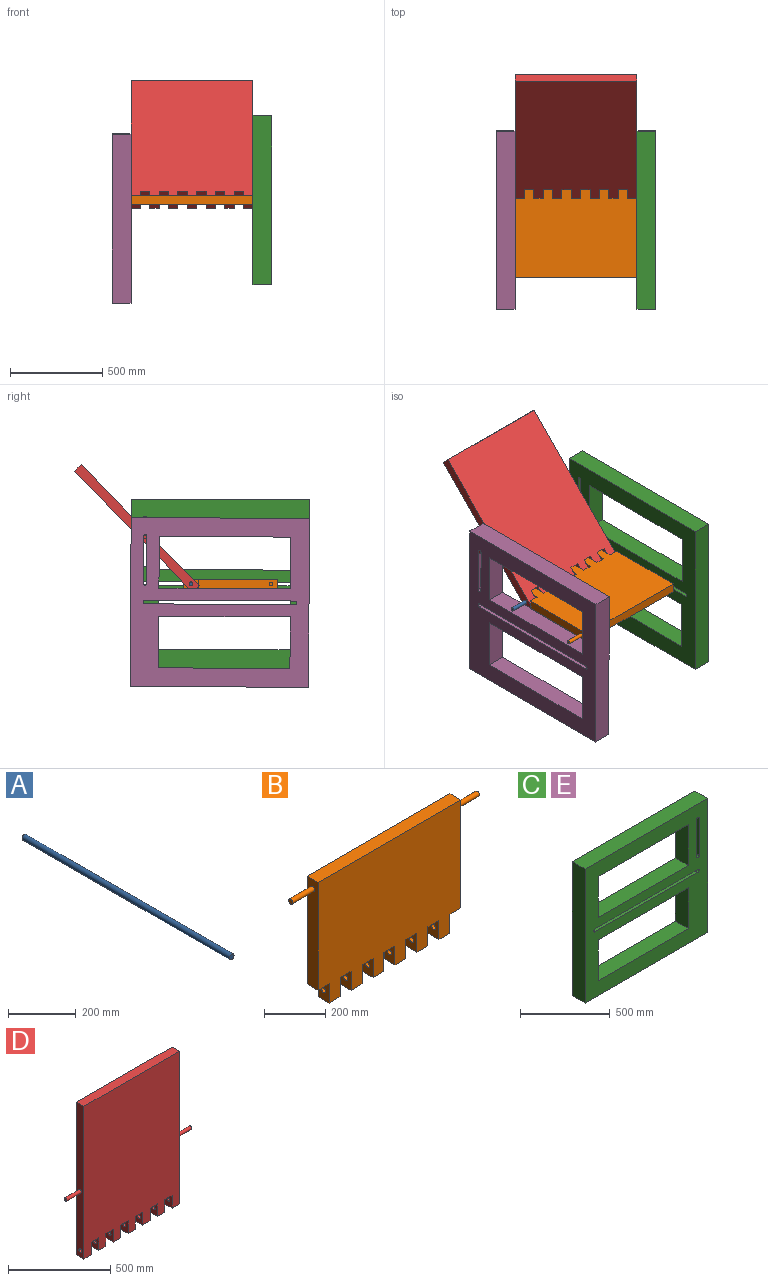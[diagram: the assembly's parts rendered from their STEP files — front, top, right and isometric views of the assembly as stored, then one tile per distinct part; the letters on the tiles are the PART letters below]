
ASSEMBLY  parts=5 mates=9
PART A: 3 faces, bbox 19.1x863.6x19.1 mm
  f0: cylinder r=9.53mm len=863.6mm, axis (0,1,0), area 51684.2mm2, adj f1,f2
  f1: plane 19.05x19.05mm, normal (0,-1,0), area 285mm2, adj f0
  f2: plane 19.05x19.05mm, normal (0,1,0), area 285mm2, adj f0
PART B: 40 faces, bbox 863.6x50.8x508 mm
  f0: plane 76.2x50.8mm, normal (1,0,0), area 3585.9mm2, adj f1,f27,f28,f29,f30
  f1: plane 50.8x50.8mm, normal (0,0,-1), area 2580.6mm2, adj f0,f2,f28,f29
  f2: plane 76.2x50.8mm, normal (-1,0,0), area 3585.9mm2, adj f1,f3,f28,f29,f35
  f3: plane 50.8x50.8mm, normal (0,0,-1), area 2580.6mm2, adj f2,f4,f28,f29
  f4: plane 76.2x50.8mm, normal (1,0,0), area 3585.9mm2, adj f3,f5,f28,f29,f35
  f5: plane 50.8x50.8mm, normal (0,0,-1), area 2580.6mm2, adj f4,f6,f28,f29
  f6: plane 76.2x50.8mm, normal (-1,0,0), area 3585.9mm2, adj f5,f7,f28,f29,f34
  f7: plane 50.8x50.8mm, normal (0,0,-1), area 2580.6mm2, adj f6,f8,f28,f29
  f8: plane 76.2x50.8mm, normal (1,0,0), area 3585.9mm2, adj f7,f9,f28,f29,f34
  f9: plane 50.8x50.8mm, normal (0,0,-1), area 2580.6mm2, adj f8,f10,f28,f29
  f10: plane 76.2x50.8mm, normal (-1,0,0), area 3585.9mm2, adj f9,f11,f28,f29,f33
  f11: plane 50.8x50.8mm, normal (0,0,-1), area 2580.6mm2, adj f10,f12,f28,f29
  f12: plane 76.2x50.8mm, normal (1,0,0), area 3585.9mm2, adj f11,f13,f28,f29,f33
  f13: plane 50.8x50.8mm, normal (0,0,-1), area 2580.6mm2, adj f12,f14,f28,f29
  f14: plane 431.8x50.8mm, normal (1,0,0), area 21650.4mm2, adj f13,f15,f28,f29,f36
  f15: plane 660.4x50.8mm, normal (0,0,1), area 33548.3mm2, adj f14,f16,f28,f29
  f16: plane 431.8x50.8mm, normal (-1,0,0), area 21650.4mm2, adj f15,f17,f28,f29,f38
  f17: plane 50.8x50.8mm, normal (0,0,-1), area 2580.6mm2, adj f16,f18,f28,f29
  f18: plane 76.2x50.8mm, normal (-1,0,0), area 3585.9mm2, adj f17,f19,f28,f29,f32
  f19: plane 50.8x50.8mm, normal (0,0,-1), area 2580.6mm2, adj f18,f20,f28,f29
  f20: plane 76.2x50.8mm, normal (1,0,0), area 3585.9mm2, adj f19,f21,f28,f29,f32
  f21: plane 50.8x50.8mm, normal (0,0,-1), area 2580.6mm2, adj f20,f22,f28,f29
  f22: plane 76.2x50.8mm, normal (-1,0,0), area 3585.9mm2, adj f21,f23,f28,f29,f31
  f23: plane 50.8x50.8mm, normal (0,0,-1), area 2580.6mm2, adj f22,f24,f28,f29
  f24: plane 76.2x50.8mm, normal (1,0,0), area 3585.9mm2, adj f23,f25,f28,f29,f31
  f25: plane 50.8x50.8mm, normal (0,0,-1), area 2580.6mm2, adj f24,f26,f28,f29
  f26: plane 76.2x50.8mm, normal (-1,0,0), area 3585.9mm2, adj f25,f27,f28,f29,f30
  f27: plane 50.8x50.8mm, normal (0,0,-1), area 2580.6mm2, adj f0,f26,f28,f29
  f28: plane 660.4x508mm, normal (0,-1,0), area 308386.5mm2, adj f0,f1,f2,f3,f4,f5,f6,f7
  f29: plane 660.4x508mm, normal (0,1,0), area 308386.5mm2, adj f0,f1,f2,f3,f4,f5,f6,f7
  f30: cylinder r=9.53mm len=50.8mm, axis (1,0,0), area 3040.2mm2, adj f0,f26
  f31: cylinder r=9.53mm len=50.8mm, axis (1,0,0), area 3040.2mm2, adj f22,f24
  f32: cylinder r=9.53mm len=50.8mm, axis (1,0,0), area 3040.2mm2, adj f18,f20
  f33: cylinder r=9.53mm len=50.8mm, axis (1,0,0), area 3040.2mm2, adj f10,f12
  f34: cylinder r=9.53mm len=50.8mm, axis (1,0,0), area 3040.2mm2, adj f6,f8
  f35: cylinder r=9.53mm len=50.8mm, axis (1,0,0), area 3040.2mm2, adj f2,f4
  f36: cylinder r=9.53mm len=101.6mm, axis (-1,0,0), area 6080.5mm2, adj f14,f37
  f37: plane 19.05x19.05mm, normal (1,0,0), area 285mm2, adj f36
  f38: cylinder r=9.53mm len=101.6mm, axis (1,0,0), area 6080.5mm2, adj f16,f39
  f39: plane 19.05x19.05mm, normal (-1,0,0), area 285mm2, adj f38
PART C: 22 faces, bbox 965.2x101.6x914.4 mm
  f0: cylinder r=9.53mm len=101.6mm, axis (0,1,0), area 3040.2mm2, adj f1,f19,f20,f21
  f1: plane 812.8x101.6mm, normal (0,0,1), area 82580.5mm2, adj f0,f2,f20,f21
  f2: cylinder r=9.53mm len=101.6mm, axis (0,1,0), area 3040.2mm2, adj f1,f19,f20,f21
  f3: plane 279.4x101.6mm, normal (-1,0,0), area 28387mm2, adj f4,f15,f20,f21
  f4: plane 711.2x101.6mm, normal (0,0,1), area 72257.9mm2, adj f3,f5,f20,f21
  f5: plane 279.4x101.6mm, normal (1,0,0), area 28387mm2, adj f4,f15,f20,f21
  f6: plane 254x101.6mm, normal (1,0,0), area 25806.4mm2, adj f7,f16,f20,f21
  f7: cylinder r=9.53mm len=101.6mm, axis (0,1,0), area 3040.2mm2, adj f6,f8,f20,f21
  f8: plane 254x101.6mm, normal (-1,0,0), area 25806.4mm2, adj f7,f16,f20,f21
  f9: plane 711.2x101.6mm, normal (0,0,1), area 72257.9mm2, adj f10,f17,f20,f21
  f10: plane 279.4x101.6mm, normal (1,0,0), area 28387mm2, adj f9,f11,f20,f21
  f11: plane 711.2x101.6mm, normal (0,0,-1), area 72257.9mm2, adj f10,f17,f20,f21
  f12: plane 914.4x101.6mm, normal (-1,0,0), area 92903mm2, adj f13,f18,f20,f21
  f13: plane 965.2x101.6mm, normal (0,0,-1), area 98064.3mm2, adj f12,f14,f20,f21
  f14: plane 914.4x101.6mm, normal (1,0,0), area 92903mm2, adj f13,f18,f20,f21
  f15: plane 711.2x101.6mm, normal (0,0,-1), area 72257.9mm2, adj f3,f5,f20,f21
  f16: cylinder r=9.53mm len=101.6mm, axis (0,1,0), area 3040.2mm2, adj f6,f8,f20,f21
  f17: plane 279.4x101.6mm, normal (-1,0,0), area 28387mm2, adj f9,f11,f20,f21
  f18: plane 965.2x101.6mm, normal (0,0,1), area 98064.3mm2, adj f12,f14,f20,f21
  f19: plane 812.8x101.6mm, normal (0,0,-1), area 82580.5mm2, adj f0,f2,f20,f21
  f20: plane 965.2x914.4mm, normal (0,-1,0), area 464267.7mm2, adj f0,f1,f2,f3,f4,f5,f6,f7
  f21: plane 965.2x914.4mm, normal (0,1,0), area 464267.7mm2, adj f0,f1,f2,f3,f4,f5,f6,f7
PART D: 41 faces, bbox 863.6x50.8x914.4 mm
  f0: plane 76.2x50.8mm, normal (-1,0,0), area 3585.9mm2, adj f1,f27,f28,f29,f36
  f1: plane 50.8x50.8mm, normal (0,0,-1), area 2580.6mm2, adj f0,f2,f28,f29
  f2: plane 76.2x50.8mm, normal (1,0,0), area 3585.9mm2, adj f1,f3,f28,f29,f36
  f3: plane 50.8x50.8mm, normal (0,0,-1), area 2580.6mm2, adj f2,f4,f28,f29
  f4: plane 76.2x50.8mm, normal (-1,0,0), area 3585.9mm2, adj f3,f5,f28,f29,f35
  f5: plane 50.8x50.8mm, normal (0,0,-1), area 2580.6mm2, adj f4,f6,f28,f29
  f6: plane 76.2x50.8mm, normal (1,0,0), area 3585.9mm2, adj f5,f7,f28,f29,f35
  f7: plane 50.8x50.8mm, normal (0,0,-1), area 2580.6mm2, adj f6,f8,f28,f29
  f8: plane 76.2x50.8mm, normal (-1,0,0), area 3585.9mm2, adj f7,f9,f28,f29,f34
  f9: plane 50.8x50.8mm, normal (0,0,-1), area 2580.6mm2, adj f8,f10,f28,f29
  f10: plane 914.4x50.8mm, normal (1,0,0), area 45881.5mm2, adj f9,f11,f28,f29,f34,f39
  f11: plane 660.4x50.8mm, normal (0,0,1), area 33548.3mm2, adj f10,f12,f28,f29
  f12: plane 914.4x50.8mm, normal (-1,0,0), area 45881.5mm2, adj f11,f13,f28,f29,f33,f37
  f13: plane 50.8x50.8mm, normal (0,0,-1), area 2580.6mm2, adj f12,f14,f28,f29
  f14: plane 76.2x50.8mm, normal (1,0,0), area 3585.9mm2, adj f13,f15,f28,f29,f33
  f15: plane 50.8x50.8mm, normal (0,0,-1), area 2580.6mm2, adj f14,f16,f28,f29
  f16: plane 76.2x50.8mm, normal (-1,0,0), area 3585.9mm2, adj f15,f17,f28,f29,f32
  f17: plane 50.8x50.8mm, normal (0,0,-1), area 2580.6mm2, adj f16,f18,f28,f29
  f18: plane 76.2x50.8mm, normal (1,0,0), area 3585.9mm2, adj f17,f19,f28,f29,f32
  f19: plane 50.8x50.8mm, normal (0,0,-1), area 2580.6mm2, adj f18,f20,f28,f29
  f20: plane 76.2x50.8mm, normal (-1,0,0), area 3585.9mm2, adj f19,f21,f28,f29,f31
  f21: plane 50.8x50.8mm, normal (0,0,-1), area 2580.6mm2, adj f20,f22,f28,f29
  f22: plane 76.2x50.8mm, normal (1,0,0), area 3585.9mm2, adj f21,f23,f28,f29,f31
  f23: plane 50.8x50.8mm, normal (0,0,-1), area 2580.6mm2, adj f22,f24,f28,f29
  f24: plane 76.2x50.8mm, normal (-1,0,0), area 3585.9mm2, adj f23,f25,f28,f29,f30
  f25: plane 50.8x50.8mm, normal (0,0,-1), area 2580.6mm2, adj f24,f26,f28,f29
  f26: plane 76.2x50.8mm, normal (1,0,0), area 3585.9mm2, adj f25,f27,f28,f29,f30
  f27: plane 50.8x50.8mm, normal (0,0,-1), area 2580.6mm2, adj f0,f26,f28,f29
  f28: plane 914.4x660.4mm, normal (0,-1,0), area 580644mm2, adj f0,f1,f2,f3,f4,f5,f6,f7
  f29: plane 914.4x660.4mm, normal (0,1,0), area 580644mm2, adj f0,f1,f2,f3,f4,f5,f6,f7
  f30: cylinder r=9.53mm len=50.8mm, axis (1,0,0), area 3040.2mm2, adj f24,f26
  f31: cylinder r=9.53mm len=50.8mm, axis (1,0,0), area 3040.2mm2, adj f20,f22
  f32: cylinder r=9.53mm len=50.8mm, axis (1,0,0), area 3040.2mm2, adj f16,f18
  f33: cylinder r=9.53mm len=50.8mm, axis (1,0,0), area 3040.2mm2, adj f12,f14
  f34: cylinder r=9.53mm len=50.8mm, axis (1,0,0), area 3040.2mm2, adj f8,f10
  f35: cylinder r=9.53mm len=50.8mm, axis (1,0,0), area 3040.2mm2, adj f4,f6
  f36: cylinder r=9.53mm len=50.8mm, axis (1,0,0), area 3040.2mm2, adj f0,f2
  f37: cylinder r=9.53mm len=101.6mm, axis (1,0,0), area 6080.5mm2, adj f12,f38
  f38: plane 19.05x19.05mm, normal (-1,0,0), area 285mm2, adj f37
  f39: cylinder r=9.53mm len=101.6mm, axis (-1,0,0), area 6080.5mm2, adj f10,f40
  f40: plane 19.05x19.05mm, normal (1,0,0), area 285mm2, adj f39
PART E: same geometry as C
PLACE A rot(axis=(0.38,0.38,-0.84),99.9deg) t=(532.87,1096.7,-452.84)mm
PLACE B rot(axis=(1,0,0),90.3deg) t=(95.26,1044.95,-427.67)mm
PLACE C rot(axis=(0,0,1),90deg) t=(431.27,459.4,-912.88)mm fixed
PLACE D rot(axis=(-1,0,0),44.3deg) t=(-229.13,1088.24,-497.84)mm
PLACE E rot(axis=(0,0,1),90deg) t=(-330.73,459.85,-1013.37)mm
MATE parallel D.f10 <-> A.f0  axis (1,0,0) through (431.27,1391.7,-150.95)mm
MATE parallel D.f10 <-> C.f21  axis (1,0,0) through (431.27,1391.7,-150.95)mm
MATE parallel E.f20 <-> C.f21  axis (1,0,0) through (-229.13,957.68,-556.47)mm
MATE parallel E.f12 <-> C.f12  axis (0,-1,0) through (-279.93,457.81,-556.17)mm
MATE planar D.f10 <-> C.f21  axis (1,0,0) through (431.27,1391.7,-150.95)mm
MATE planar D.f10 <-> B.f14  axis (1,0,0) through (431.27,1391.7,-150.95)mm
MATE parallel C.f13 <-> E.f13  axis (0,0,-1) through (482.07,942,-910.74)mm
MATE parallel C.f21 <-> E.f20  axis (-1,0,0) through (431.27,957.23,-455.99)mm
MATE parallel C.f21 <-> E.f20  axis (-1,0,0) through (431.27,1270.5,-528.27)mm
